# Revit family: 22470CHN
name_source: partatom
category: Plumbing Fixtures
units: mm (PartAtom-declared; Revit-internal decimal feet)

## family parameters
Always vertical = No
Cut with Voids When Loaded = No
Maintain Annotation Orientation = No
OmniClass Number = 23.31.19.00
OmniClass Title = Toilets
Part Type = Normal
Room Calculation Point = No
Round Connector Dimension = Use Diameter
Shared = No
Work Plane-Based = Yes

## types (1)
- 007 White
    Connector Description = Water Outlet 110 mm
    Default Elevation = 1219 mm
    Description = LavaPura Element S Wall hung Shower Toilet B Autolid
    Diameter = 110 mm  [stored 0.360892 ft]
    Manufacturer = Hansgrohe
    Material = Hansgrohe - Ceramic - 007 White
    Material 1 = Hansgrohe - Plastic - Matte White
    Material 2 = Hansgrohe - Plastic - Graphite
    Model = 22470CHN
    Product Page URL = https://www.hansgrohe.com
    Product data url = https://bimobject.com
    URL = https://www.hansgrohe.com
    Version = 1

note: [stored X ft] marks values corroborated as IEEE doubles in the binary element streams (Revit-internal decimal feet)

## geometry (parser evidence)
native form markers: Sweep x1
no freeform markers — native parametric forms only
